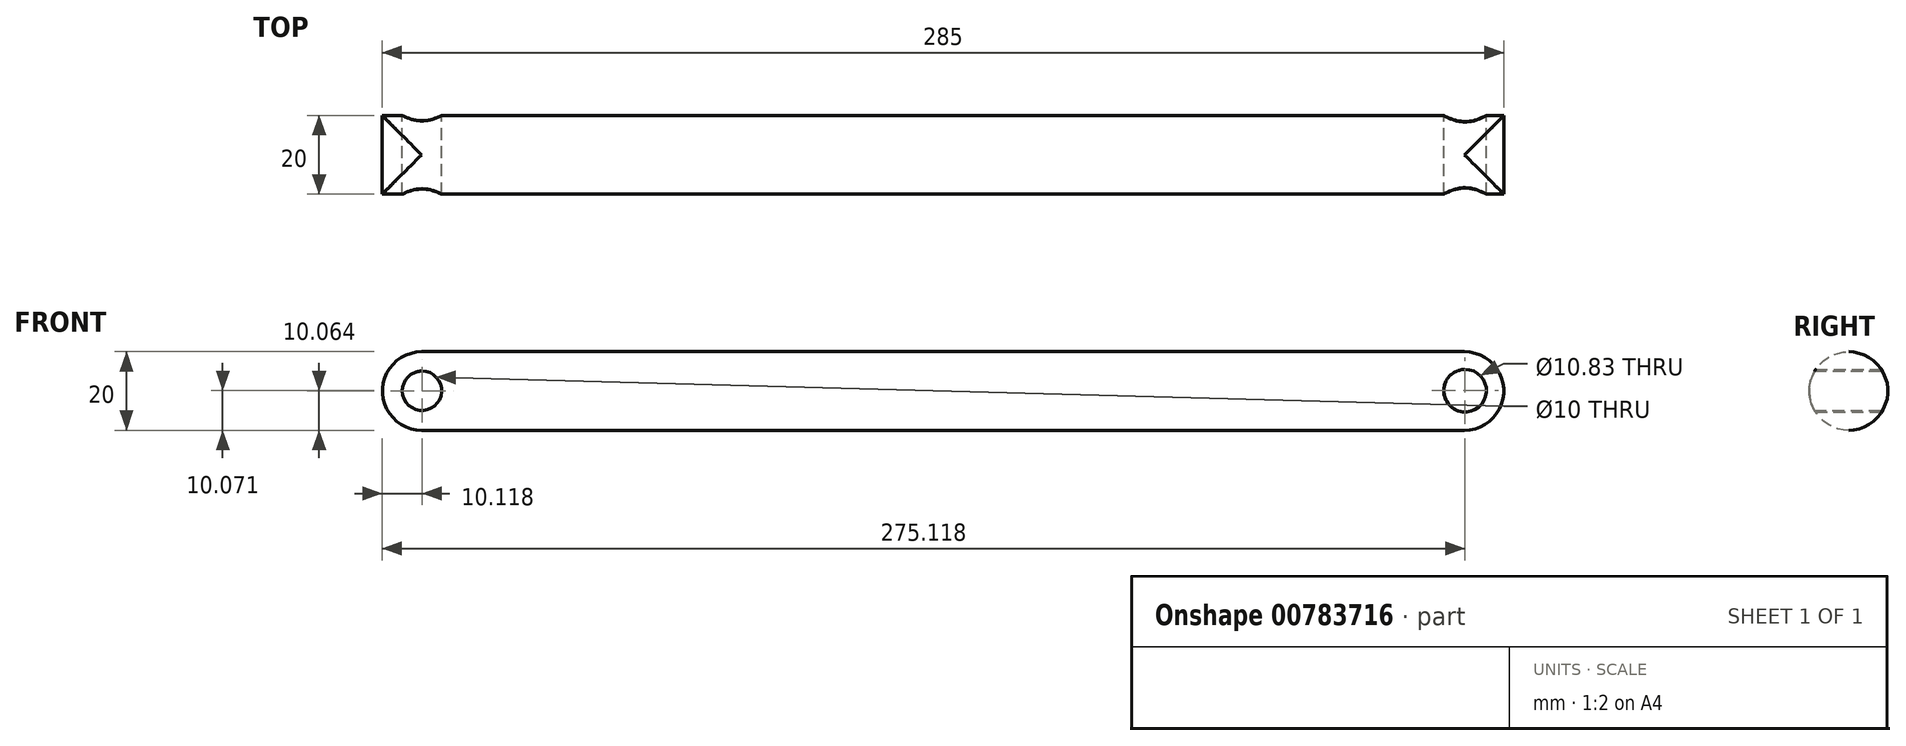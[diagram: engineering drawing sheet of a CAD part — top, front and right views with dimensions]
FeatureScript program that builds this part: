
annotation { "Feature Type Name" : "Feature", "Feature Type Description" : "" }
export const myFeature = defineFeature(function(context is Context, id is Id, definition is map)
    precondition{}
    {
        {
            var Q0;
            Q0=qCreatedBy(makeId("Front.planeOp"),FACE);
            var sketch = newSketch(context, id + "F0", { "sketchPlane" : qUnion([Q0])});
            skLineSegment(sketch, "E0.bottom", {"start": v(-285, 20) * mm, "end": v(0, 20) * mm});
            skLineSegment(sketch, "E0.top", {"start": v(-285, 0) * mm, "end": v(0, 0) * mm});
            skLineSegment(sketch, "E0.left", {"start": v(-285, 20) * mm, "end": v(-285, 0) * mm});
            skLineSegment(sketch, "E0.right", {"start": v(0, 20) * mm, "end": v(0, 0) * mm});
            skSolve(sketch);
        }
        {
            var Q0;
            Q0=makeQuery(id+"F0.imprint","IMPRINT",FACE,{"disambiguationData":[TD([[makeQuery(id+"F0.imprint","IMPRINT",EDGE,{"derivedFrom":sQuery(id+"F0.wireOp",EDGE,"E0.bottom")}),-1.0]])]});
            extrude(context, id + "F1", {"entities" : qUnion([Q0]), "depth" : 20 * mm, "offsetDistance" : 25 * mm});
        }
        {
            var Q0;
            Q0=makeQuery(id+"F1.opExtrude","CAP_EDGE",EDGE,{"disambiguationData":[OSD([sQuery(id+"F0.wireOp",EDGE,"E0.bottom")])],"isStart":false});
            var Q1;
            Q1=makeQuery(id+"F1.opExtrude","CAP_EDGE",EDGE,{"disambiguationData":[OSD([sQuery(id+"F0.wireOp",EDGE,"E0.bottom")])],"isStart":true});
            var Q2;
            Q2=makeQuery(id+"F1.opExtrude","CAP_EDGE",EDGE,{"disambiguationData":[OSD([sQuery(id+"F0.wireOp",EDGE,"E0.top")])],"isStart":false});
            var Q3;
            Q3=makeQuery(id+"F1.opExtrude","SWEPT_EDGE",EDGE,{"disambiguationData":[OSD([sQuery(id+"F0.wireOp",EDGE,"E0.top"),sQuery(id+"F0.wireOp",EDGE,"E0.right")])]});
            var Q4;
            Q4=makeQuery(id+"F1.opExtrude","CAP_EDGE",EDGE,{"disambiguationData":[OSD([sQuery(id+"F0.wireOp",EDGE,"E0.top")])],"isStart":true});
            var Q5;
            Q5=makeQuery(id+"F1.opExtrude","SWEPT_FACE",FACE,{"disambiguationData":[OSD([sQuery(id+"F0.wireOp",EDGE,"E0.top")])]});
            var Q6;
            Q6=makeQuery(id+"F1.opExtrude","SWEPT_EDGE",EDGE,{"disambiguationData":[OSD([sQuery(id+"F0.wireOp",EDGE,"E0.bottom"),sQuery(id+"F0.wireOp",EDGE,"E0.right")])]});
            var Q7;
            Q7=makeQuery(id+"F1.opExtrude","SWEPT_EDGE",EDGE,{"disambiguationData":[OSD([sQuery(id+"F0.wireOp",EDGE,"E0.bottom"),sQuery(id+"F0.wireOp",EDGE,"E0.left")])]});
            fillet(context, id + "F2", {"entities" : qUnion([Q0, Q1, Q2, Q3, Q4, Q5, Q6, Q7]), "radius" : 10 * mm, "tangentPropagation" : true, "allowEdgeOverflow" : false});
        }
        {
            var Q0;
            Q0=qCreatedBy(makeId("Front.planeOp"),FACE);
            var sketch = newSketch(context, id + "F3", { "sketchPlane" : qUnion([Q0])});
            skCircle(sketch, "E1", {"center": v(-274.88, 10.06) * mm, "radius": 5 * mm});
            skCircle(sketch, "E2", {"center": v(-9.88, 10.07) * mm, "radius": 5.41 * mm});
            skSolve(sketch);
        }
        {
            var Q0;
            Q0 = qSketchRegion(id + "F3", true);
            extrude(context, id + "F4", {"entities" : qUnion([Q0]), "operationType" : NewBodyOperationType.REMOVE, "depth" : 20 * mm, "offsetDistance" : 25 * mm});
        }
    });
